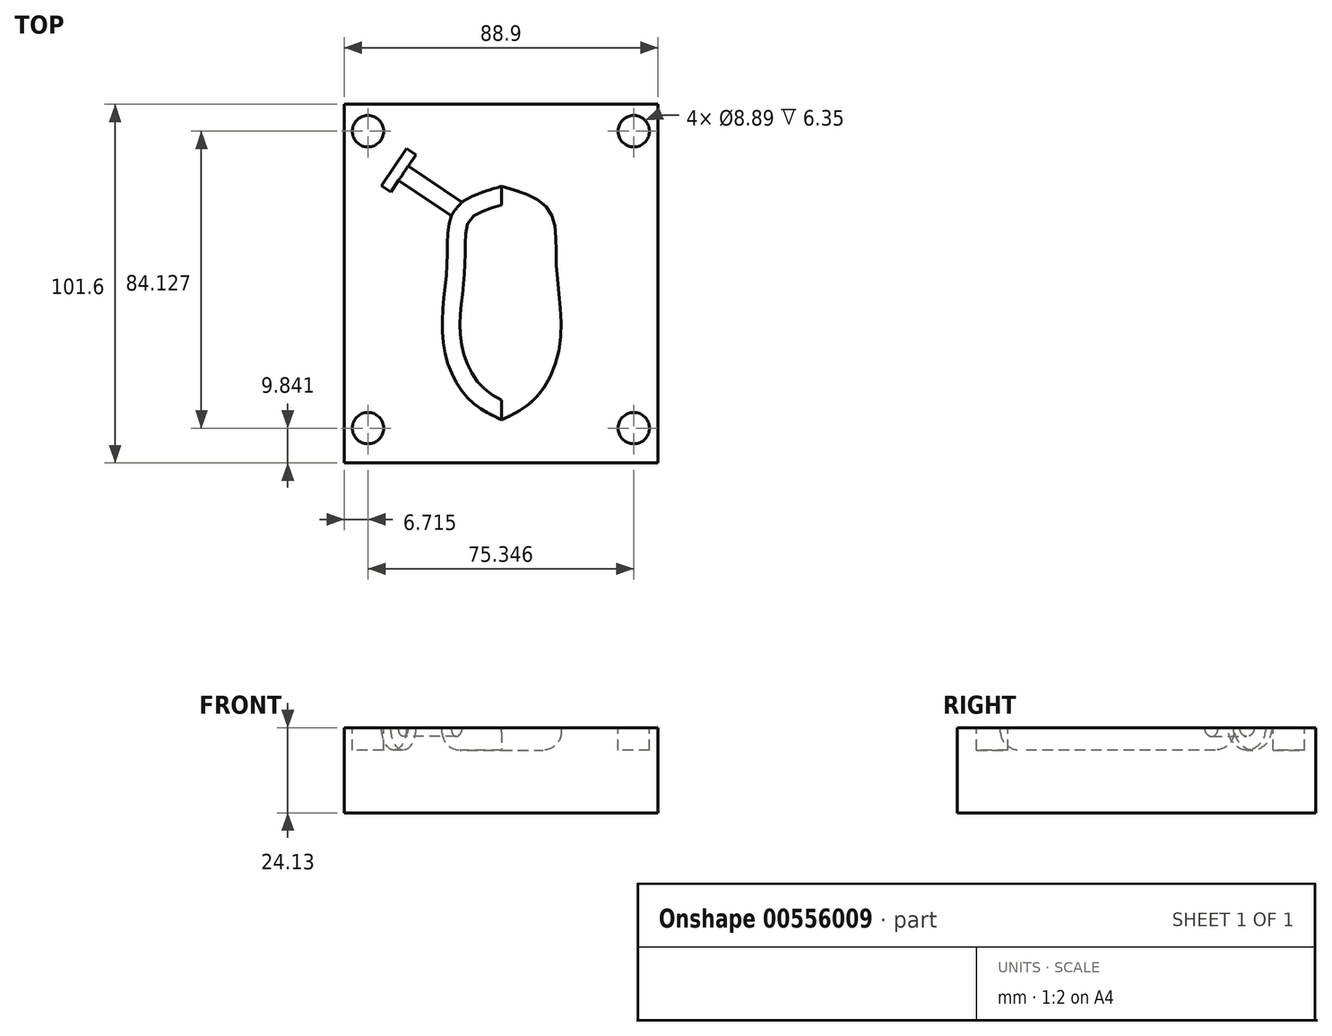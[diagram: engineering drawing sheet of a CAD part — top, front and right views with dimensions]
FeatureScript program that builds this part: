
annotation { "Feature Type Name" : "Feature", "Feature Type Description" : "" }
export const myFeature = defineFeature(function(context is Context, id is Id, definition is map)
    precondition{}
    {
        {
            var Q0;
            Q0=qCreatedBy(makeId("Front.planeOp"),FACE);
            var sketch = newSketch(context, id + "F0", { "sketchPlane" : qUnion([Q0])});
            skLineSegment(sketch, "E0", {"start": v(-44.6, -0.06) * mm, "end": v(44.3, -0.06) * mm});
            skLineSegment(sketch, "E1", {"start": v(44.3, -0.06) * mm, "end": v(44.3, -24.19) * mm});
            skLineSegment(sketch, "E2", {"start": v(44.3, -24.19) * mm, "end": v(-44.6, -24.19) * mm});
            skLineSegment(sketch, "E3", {"start": v(-44.6, -0.06) * mm, "end": v(-44.6, -24.19) * mm});
            skSolve(sketch);
        }
        {
            var Q0;
            Q0=qSketchRegion(id+"F0",true);
            extrude(context, id + "F1", {"entities" : qUnion([Q0]), "depth" : 50.8 * mm, "offsetDistance" : 25.4 * mm, "hasSecondDirection" : true, "secondDirectionOppositeDirection" : true, "secondDirectionDepth" : 50.8 * mm});
        }
        {
            var Q0;
            Q0=makeQuery(id+"F1.opExtrude","SWEPT_FACE",FACE,{"disambiguationData":[OSD([sQuery(id+"F0.wireOp",EDGE,"E0")])]});
            var sketch = newSketch(context, id + "F2", { "sketchPlane" : qUnion([Q0])});
            skCircle(sketch, "E4", {"center": v(-37.9, 43.17) * mm, "radius": 4.45 * mm});
            skCircle(sketch, "E5", {"center": v(-37.9, -40.96) * mm, "radius": 4.45 * mm});
            skCircle(sketch, "E6", {"center": v(37.45, 43.17) * mm, "radius": 4.45 * mm});
            skCircle(sketch, "E7", {"center": v(37.45, -40.96) * mm, "radius": 4.45 * mm});
            skSolve(sketch);
        }
        {
            var Q0;
            Q0=qSketchRegion(id+"F2",true);
            extrude(context, id + "F3", {"entities" : qUnion([Q0]), "operationType" : NewBodyOperationType.REMOVE, "oppositeDirection" : true, "depth" : 6.35 * mm, "offsetDistance" : 25.4 * mm});
        }
        {
            var Q0;
            Q0=makeQuery(id+"F1.opExtrude","SWEPT_FACE",FACE,{"disambiguationData":[OSD([sQuery(id+"F0.wireOp",EDGE,"E0")])]});
            var sketch = newSketch(context, id + "F4", { "sketchPlane" : qUnion([Q0])});
            skSolve(sketch);
        }
        {
            var Q0;
            {var subQ0=sQuery(id+"F0.wireOp",EDGE,"E0");Q0=makeQuery(id+"F4.imprint","IMPRINT",FACE,{"disambiguationData":[TD([[makeQuery(id+"F4.imprint","IMPRINT",EDGE,{"derivedFrom":makeQuery(id+"F1.opExtrude","CAP_EDGE",EDGE,{"disambiguationData":[OSD([subQ0])],"isStart":true})}),-1.0]])]});}
            var sketch = newSketch(context, id + "F5", { "sketchPlane" : qUnion([Q0])});
            skLineSegment(sketch, "E8", {"start": v(0, -30.21) * mm, "end": v(0, 37.81) * mm, "construction": true});
            skFitSpline(sketch, "E9", {"points": [v(0, -38.6) * mm, v(-9.67, -32.31) * mm, v(-16.66, -16.24) * mm, v(-15.5, 5.43) * mm, v(-13.4, 20.8) * mm, v(0, 27.56) * mm], "startDerivative": vector(-60.26, 28.6) * mm, "endDerivative": vector(85.1, 24.6) * mm});
            skFitSpline(sketch, "E10.MirrorCS", {"points": [v(0, -38.6) * mm, v(9.67, -32.31) * mm, v(16.66, -16.24) * mm, v(15.5, 5.43) * mm, v(13.4, 20.8) * mm, v(0, 27.56) * mm], "startDerivative": vector(60.26, 28.6) * mm, "endDerivative": vector(-85.1, 24.6) * mm});
            skSolve(sketch);
        }
        {
            var Q0;
            Q0=qSketchRegion(id+"F5",true);
            extrude(context, id + "F6", {"entities" : qUnion([Q0]), "operationType" : NewBodyOperationType.REMOVE, "oppositeDirection" : true, "depth" : 6.35 * mm, "offsetDistance" : 25.4 * mm});
        }
        {
            var Q0;
            {var subQ0=sQuery(id+"F0.wireOp",EDGE,"E0");Q0=makeQuery(id+"F4.imprint","IMPRINT",FACE,{"disambiguationData":[TD([[makeQuery(id+"F4.imprint","IMPRINT",EDGE,{"derivedFrom":makeQuery(id+"F1.opExtrude","CAP_EDGE",EDGE,{"disambiguationData":[OSD([subQ0])],"isStart":true})}),-1.0]])]});}
            var sketch = newSketch(context, id + "F7", { "sketchPlane" : qUnion([Q0])});
            skLineSegment(sketch, "E11", {"start": v(-6.11, 16.73) * mm, "end": v(-30.78, 33.18) * mm});
            skSolve(sketch);
        }
        {
            var Q0;
            Q0=sQuery(id+"F7.wireOp",EDGE,"E11");
            cPlane(context, id + "F8", {"entities" : qUnion([Q0]), "cplaneType" : CPlaneType.LINE_ANGLE, "offset" : 25.4 * mm, "angle" : 0 * degree, "width" : 152.4 * mm, "height" : 152.4 * mm});
        }
        {
            var Q0;
            Q0=qCreatedBy(id+"F8.planeOp",FACE);
            var sketch = newSketch(context, id + "F9", { "sketchPlane" : qUnion([Q0])});
            skLineSegment(sketch, "E12", {"start": v(-21.48, -0.06) * mm, "end": v(-43.7, -0.06) * mm});
            skLineSegment(sketch, "E13", {"start": v(-43.7, -0.06) * mm, "end": v(-43.7, -6.4) * mm});
            skLineSegment(sketch, "E14", {"start": v(-43.7, -6.4) * mm, "end": v(-40.53, -6.4) * mm});
            skLineSegment(sketch, "E15", {"start": v(-40.53, -6.4) * mm, "end": v(-40.53, -2.53) * mm});
            skLineSegment(sketch, "E16", {"start": v(-40.53, -2.53) * mm, "end": v(-21.48, -2.53) * mm});
            skLineSegment(sketch, "E17", {"start": v(-21.48, -2.53) * mm, "end": v(-21.48, -0.06) * mm});
            skSolve(sketch);
        }
        {
            var Q0;
            Q0=qSketchRegion(id+"F9",true);
            var Q1;
            Q1=sQuery(id+"F7.wireOp",EDGE,"E11");
            revolve(context, id + "F10", {"operationType" : NewBodyOperationType.REMOVE, "entities" : qUnion([Q0]), "axis" : qUnion([Q1]), "revolveType" : RevolveType.FULL, "oppositeDirection" : true});
        }
        {
            var Q0;
            Q0=makeQuery(id+"F6.boolean.opBoolean","COPY",EDGE,{"derivedFrom":makeQuery(id+"F6.opExtrude","CAP_EDGE",EDGE,{"disambiguationData":[OSD([sQuery(id+"F5.wireOp",EDGE,"E9")])],"isStart":false})});
            var Q1;
            Q1=makeQuery(id+"F6.boolean.opBoolean","COPY",EDGE,{"derivedFrom":makeQuery(id+"F6.opExtrude","CAP_EDGE",EDGE,{"disambiguationData":[OSD([sQuery(id+"F5.wireOp",EDGE,"E10.MirrorCS")])],"isStart":false})});
            fillet(context, id + "F11", {"entities" : qUnion([Q0, Q1]), "radius" : 5.08 * mm, "tangentPropagation" : true, "allowEdgeOverflow" : false});
        }
    });
